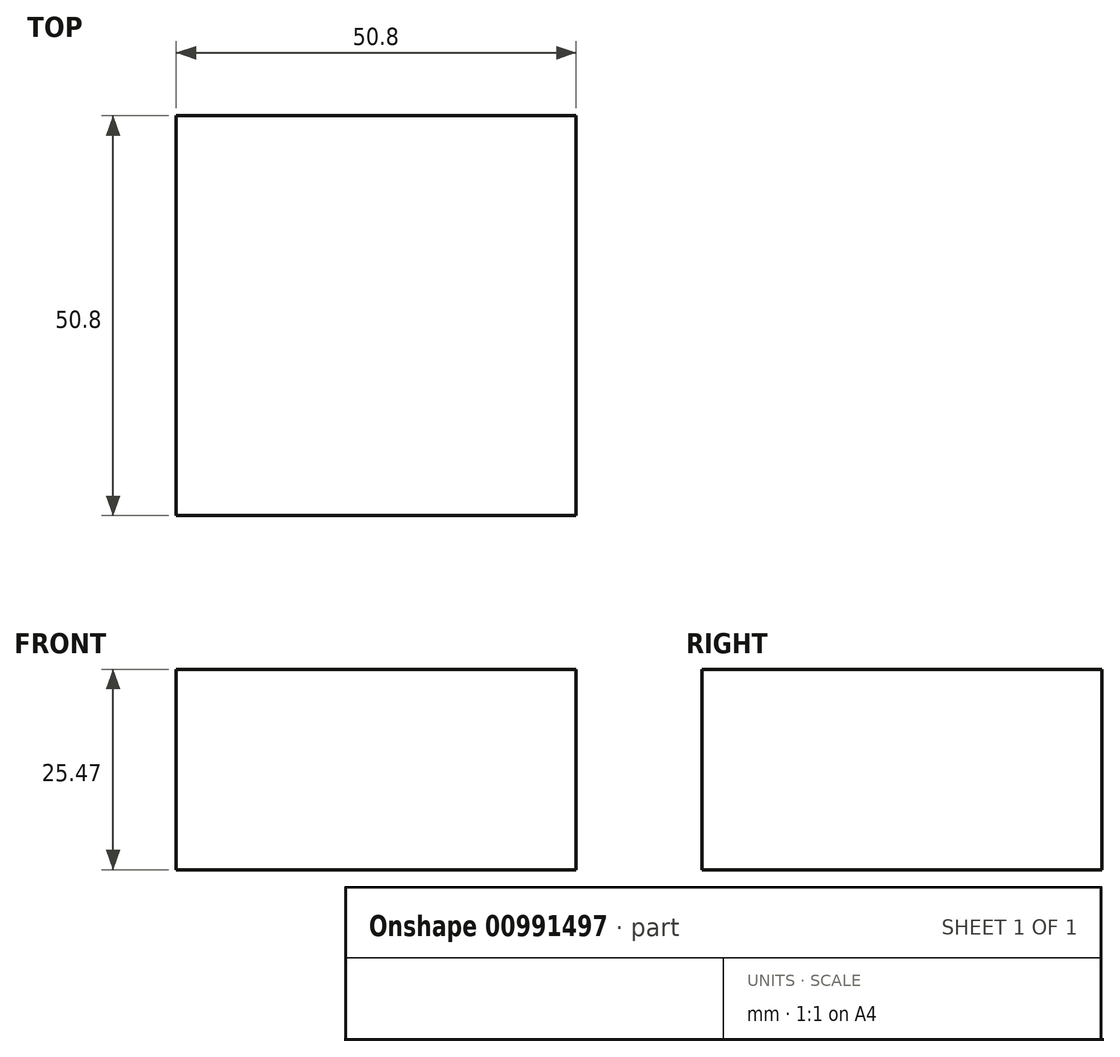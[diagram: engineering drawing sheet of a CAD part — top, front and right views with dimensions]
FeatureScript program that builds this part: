
annotation { "Feature Type Name" : "Feature", "Feature Type Description" : "" }
export const myFeature = defineFeature(function(context is Context, id is Id, definition is map)
    precondition{}
    {
        {
            var Q0;
            Q0=qCreatedBy(makeId("Front.planeOp"),FACE);
            var sketch = newSketch(context, id + "F0", { "sketchPlane" : qUnion([Q0])});
            skLineSegment(sketch, "E0", {"start": v(0, 0) * mm, "end": v(50.8, 0) * mm});
            skLineSegment(sketch, "E1", {"start": v(0, 0) * mm, "end": v(0, 25.47) * mm});
            skLineSegment(sketch, "E2", {"start": v(0, 25.47) * mm, "end": v(50.8, 25.47) * mm});
            skLineSegment(sketch, "E3", {"start": v(50.8, 25.47) * mm, "end": v(50.8, 0) * mm});
            skSolve(sketch);
        }
        {
            var Q0;
            Q0=makeQuery(id+"F0.imprint","IMPRINT",FACE,{"disambiguationData":[TD([[makeQuery(id+"F0.imprint","IMPRINT",EDGE,{"derivedFrom":sQuery(id+"F0.wireOp",EDGE,"E0")}),1.0]])]});
            extrude(context, id + "F1", {"entities" : qUnion([Q0]), "depth" : 50.8 * mm, "offsetDistance" : 25.4 * mm});
        }
    });
